# Revit family: Loops Family
name_source: partatom
category: Furniture
revit_build: Autodesk Revit 2018 (Build: 20170223_1515(x64)
units: mm (PartAtom-declared; Revit-internal decimal feet)

## family parameters
Always vertical = Yes
Cut with Voids When Loaded = No
OmniClass Number = 23.40.20.00
OmniClass Title = General Furniture and Specialties
Room Calculation Point = No
Shared = No
Work Plane-Based = No

## types (14) — shared parameters

## per-type parameters (varying)
| type | FurnitureType |
| Lounge Chair (770X680X785X420) | Loops Range Family : Lounge Chair (Armless) |
| Lounge Chair With Arms (770X680X785X420) | Loops Range Family : Lounge Chair (With Arms) |
| Sofa (1600X680X785X420) | Loops Range Family : Sofa (No Arms)1600X680X785 |
| Sofa With Arms (1600X680X785X420) | Loops Range Family : Sofa (arms) 1600X680X785 |
| Stool (500X450X450X450) | Loops Range Family : Stool 500X450X450 |
| Bench (1600X440X450X450) | Loops Range Family : Bench 1600X440X450 |
| Dining Table (1400X800X730) | Loops Range Family : Dining Table 1400X800X730 |
| Dining Table (1800X800X730) | Loops Range Family : Dining Table 1800X800X730 |
| Side Table Round (450X450X500) | Loops Range Family : Side Table Round 450X450X500 |
| Side Table Loop (800X450X500) | Loops Range Family : Side Table 800X450X500 |
| Side Table Loop (1200X400X500) | Loops Range Family : Side Table 1200X400X500 |
| Coffee Table Round (450X450X370) | Loops Range Family : Coffee Table Round 450X450X370 |
| Coffee Table Loop (800X450X370) | Loops Range Family : Coffee Table 800X450X370 |
| Coffee Table Loop (1200X400X370) | Loops Range Family : Coffee Table 1200X400X370 |

## geometry (parser evidence)
native form markers: Sweep x36
no freeform markers — native parametric forms only
